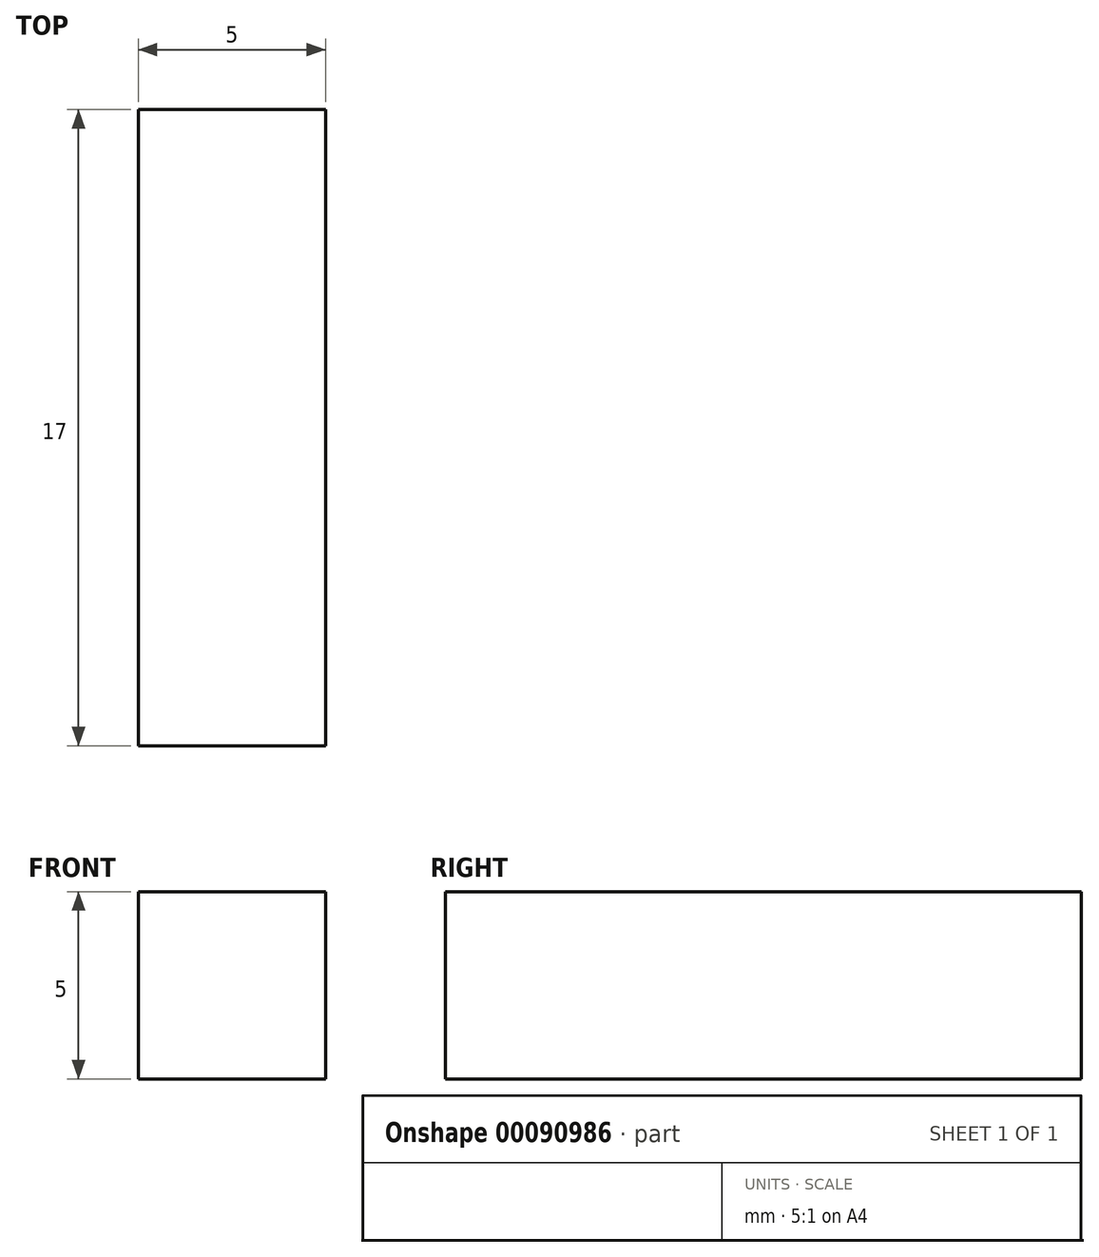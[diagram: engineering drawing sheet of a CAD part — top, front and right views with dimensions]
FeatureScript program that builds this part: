
annotation { "Feature Type Name" : "Feature", "Feature Type Description" : "" }
export const myFeature = defineFeature(function(context is Context, id is Id, definition is map)
    precondition{}
    {
        {
            var Q0;
            Q0=qCreatedBy(makeId("Front.planeOp"),FACE);
            var sketch = newSketch(context, id + "F0", { "sketchPlane" : qUnion([Q0])});
            skLineSegment(sketch, "E0.bottom", {"start": v(-33.74, 30.37) * mm, "end": v(-28.74, 30.37) * mm});
            skLineSegment(sketch, "E0.top", {"start": v(-33.74, 25.37) * mm, "end": v(-28.74, 25.37) * mm});
            skLineSegment(sketch, "E0.left", {"start": v(-33.74, 30.37) * mm, "end": v(-33.74, 25.37) * mm});
            skLineSegment(sketch, "E0.right", {"start": v(-28.74, 30.37) * mm, "end": v(-28.74, 25.37) * mm});
            skSolve(sketch);
        }
        {
            var Q0;
            Q0=makeQuery(id+"F0.imprint","IMPRINT",FACE,{"disambiguationData":[TD([[makeQuery(id+"F0.imprint","IMPRINT",EDGE,{"derivedFrom":sQuery(id+"F0.wireOp",EDGE,"E0.bottom")}),-1.0]])]});
            extrude(context, id + "F1", {"entities" : qUnion([Q0]), "depth" : 17 * mm});
        }
    });
